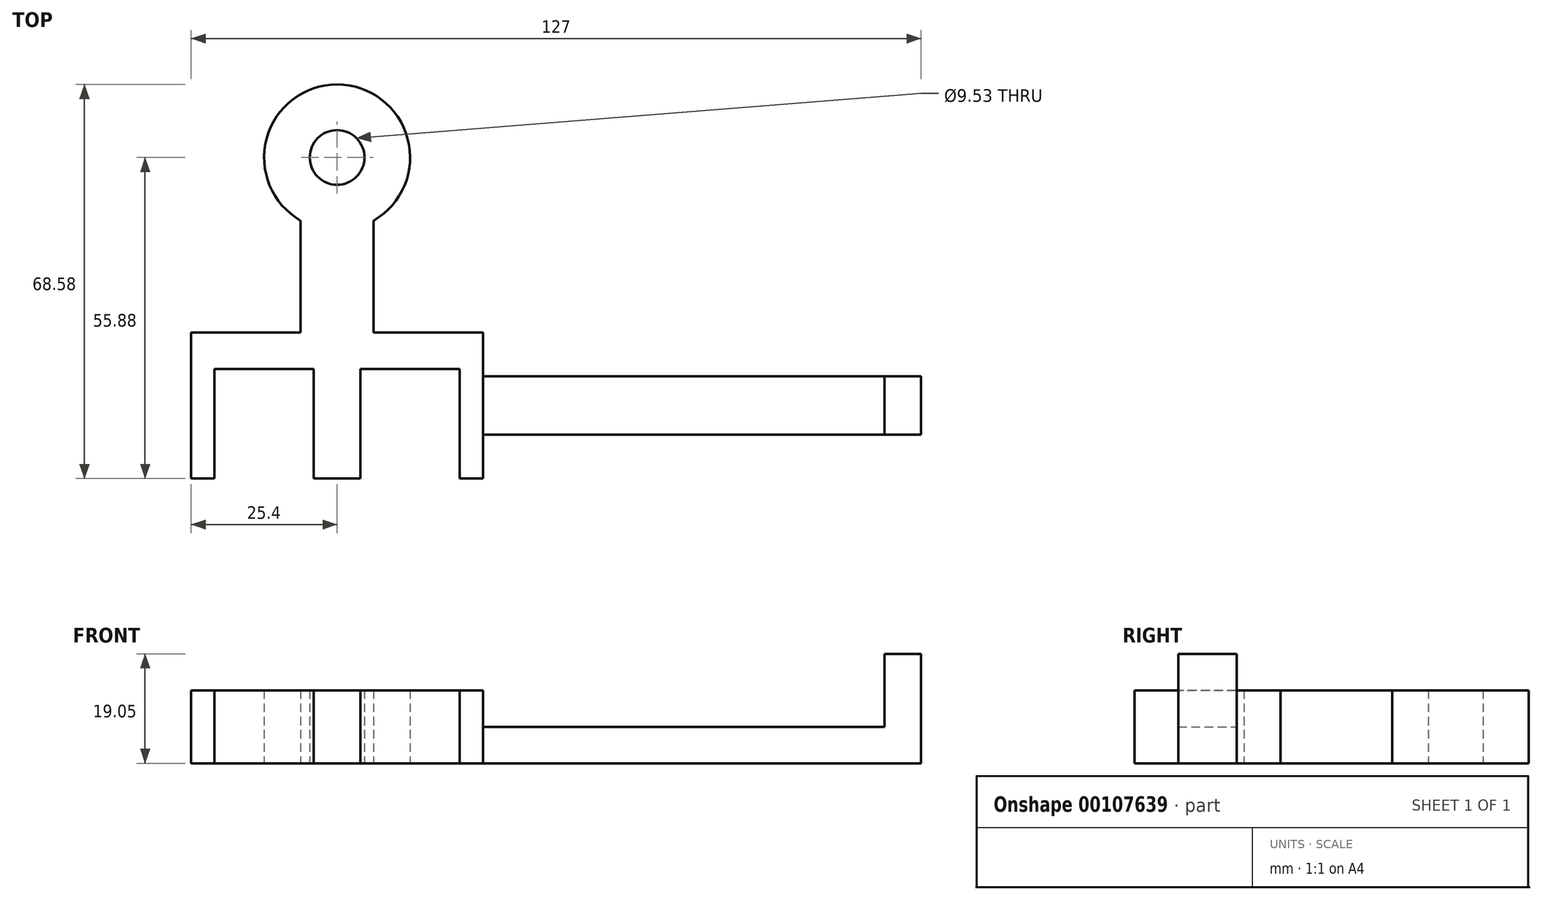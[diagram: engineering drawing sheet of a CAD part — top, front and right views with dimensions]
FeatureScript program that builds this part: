
annotation { "Feature Type Name" : "Feature", "Feature Type Description" : "" }
export const myFeature = defineFeature(function(context is Context, id is Id, definition is map)
    precondition{}
    {
        {
            var Q0;
            Q0=qCreatedBy(makeId("Top.planeOp"),FACE);
            var sketch = newSketch(context, id + "F0", { "sketchPlane" : qUnion([Q0])});
            skLineSegment(sketch, "E0", {"start": v(-50.8, 0) * mm, "end": v(-50.8, 25.4) * mm});
            skLineSegment(sketch, "E1", {"start": v(-50.8, 25.4) * mm, "end": v(0, 25.4) * mm});
            skLineSegment(sketch, "E2", {"start": v(0, 25.4) * mm, "end": v(0, 0) * mm});
            skLineSegment(sketch, "E3", {"start": v(0, 0) * mm, "end": v(-50.8, 0) * mm});
            skCircle(sketch, "E4", {"center": v(-25.4, 55.88) * mm, "radius": 4.76 * mm});
            skCircle(sketch, "E5", {"center": v(-25.4, 55.88) * mm, "radius": 12.7 * mm});
            skLineSegment(sketch, "E6", {"start": v(-31.75, 44.88) * mm, "end": v(-31.75, 25.4) * mm});
            skLineSegment(sketch, "E7.MirrorCS", {"start": v(-19.05, 44.88) * mm, "end": v(-19.05, 25.4) * mm});
            skLineSegment(sketch, "E8", {"start": v(-46.74, 0) * mm, "end": v(-46.74, 19.05) * mm});
            skLineSegment(sketch, "E9", {"start": v(-29.46, 19.05) * mm, "end": v(-29.46, 0) * mm});
            skLineSegment(sketch, "E10", {"start": v(-46.74, 19.05) * mm, "end": v(-29.46, 19.05) * mm});
            skLineSegment(sketch, "E11.MirrorCS", {"start": v(-21.34, 19.05) * mm, "end": v(-21.34, 0) * mm});
            skLineSegment(sketch, "E12.MirrorCS", {"start": v(-4.06, 19.05) * mm, "end": v(-21.34, 19.05) * mm});
            skLineSegment(sketch, "E13.MirrorCS", {"start": v(-4.06, 0) * mm, "end": v(-4.06, 19.05) * mm});
            skSolve(sketch);
        }
        {
            var Q0;
            {var subQ0=sQuery(id+"F0.wireOp",EDGE,"E6");Q0=makeQuery(id+"F0.imprint","IMPRINT",FACE,{"disambiguationData":[TD([[makeQuery(id+"F0.imprint","IMPRINT",EDGE,{"derivedFrom":subQ0}),1.0]])]});}
            var Q1;
            Q1=makeQuery(id+"F0.imprint","IMPRINT",FACE,{"disambiguationData":[TD([[makeQuery(id+"F0.imprint","IMPRINT",EDGE,{"derivedFrom":sQuery(id+"F0.wireOp",EDGE,"E4")}),-1.0]])]});
            var Q2;
            {var subQ4=sQuery(id+"F0.wireOp",EDGE,"E0");Q2=makeQuery(id+"F0.imprint","IMPRINT",FACE,{"disambiguationData":[TD([[makeQuery(id+"F0.imprint","IMPRINT",EDGE,{"derivedFrom":subQ4}),-1.0]])]});}
            extrude(context, id + "F1", {"entities" : qUnion([Q0, Q1, Q2]), "depth" : 12.7 * mm});
        }
        {
            var Q0;
            Q0=makeQuery(id+"F1.opExtrude","SWEPT_FACE",FACE,{"disambiguationData":[OSD([sQuery(id+"F0.wireOp",EDGE,"E2")])]});
            var sketch = newSketch(context, id + "F2", { "sketchPlane" : qUnion([Q0])});
            skLineSegment(sketch, "E14", {"start": v(7.62, 0) * mm, "end": v(17.78, 0) * mm});
            skLineSegment(sketch, "E15", {"start": v(7.62, 6.35) * mm, "end": v(17.78, 6.35) * mm});
            skLineSegment(sketch, "E16", {"start": v(7.62, 6.35) * mm, "end": v(7.62, 0) * mm});
            skLineSegment(sketch, "E17", {"start": v(17.78, 6.35) * mm, "end": v(17.78, 0) * mm});
            skSolve(sketch);
        }
        {
            var Q0;
            Q0=makeQuery(id+"F2.imprint","IMPRINT",FACE,{"disambiguationData":[TD([[makeQuery(id+"F2.imprint","IMPRINT",EDGE,{"derivedFrom":sQuery(id+"F2.wireOp",EDGE,"E14")}),-1.0]])]});
            extrude(context, id + "F3", {"entities" : qUnion([Q0]), "operationType" : NewBodyOperationType.ADD, "depth" : 76.2 * mm});
        }
        {
            var Q0;
            Q0=makeQuery(id+"F3.opExtrude","SWEPT_FACE",FACE,{"disambiguationData":[OSD([sQuery(id+"F2.wireOp",EDGE,"E15")])]});
            var sketch = newSketch(context, id + "F4", { "sketchPlane" : qUnion([Q0])});
            skLineSegment(sketch, "E18", {"start": v(69.85, 17.78) * mm, "end": v(69.85, 7.62) * mm});
            skLineSegment(sketch, "E19", {"start": v(69.85, 7.62) * mm, "end": v(76.2, 7.62) * mm});
            skLineSegment(sketch, "E20", {"start": v(76.2, 7.62) * mm, "end": v(76.2, 17.78) * mm});
            skLineSegment(sketch, "E21", {"start": v(76.2, 17.78) * mm, "end": v(69.85, 17.78) * mm});
            skSolve(sketch);
        }
        {
            var Q0;
            Q0=makeQuery(id+"F4.imprint","IMPRINT",FACE,{"disambiguationData":[TD([[makeQuery(id+"F4.imprint","IMPRINT",EDGE,{"derivedFrom":sQuery(id+"F4.wireOp",EDGE,"E18")}),1.0]])]});
            extrude(context, id + "F5", {"entities" : qUnion([Q0]), "operationType" : NewBodyOperationType.ADD, "depth" : 12.7 * mm});
        }
    });
